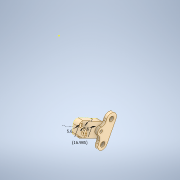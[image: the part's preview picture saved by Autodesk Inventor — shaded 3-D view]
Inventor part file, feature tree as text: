
AUTODESK INVENTOR PART (.ipt)
format: ipt  version: 2020 (Build 240168000, 168)  size: 313,344 bytes
history: native  units: in
note: dims shown in document units (in); Inventor stores cm internally (conversion verified against a paired STEP export)
features: sketch x11, extrude x7, fillet x4, projected_geometry x2
ambient origin geometry x8: Origin, YZ Plane, XZ Plane, XY Plane, X Axis, Y Axis, Z Axis, Center Point
bodies: Body1 (feature_tree)
feature tree (24):
  sketch  "Sketch3"  dims[d0=0.0039in d1=0.2362in d2=0.0in]
  sketch  "Sketch4"  dims[d3=0.315in d4=0.1575in d5=0.315in d6=0.0787in d7=0.0in d8=0.1181in]
  extrude  "Extrusion1"  Depth=0.2362in TaperAngle=0.0deg
  extrude  "Extrusion2"  Depth=0.1575in
  fillet  "Fillet1"  Radius=0.315in
  sketch  "Sketch7"  dims[d13=0.0787in d14=0.0787in d15=0.0in d16=0.2008in]
  fillet  "Fillet2"  Radius=0.0787in
  fillet  "Fillet3"  Radius=0.1181in
  extrude  "Extrusion3"  Depth=0.1181in
  extrude  "Extrusion4"  Depth=0.0787in
  sketch  "Sketch9"  dims[d22=0.3717in d23=0.0787in]
  sketch  "Sketch10"  dims[d27=0.1181in]
  sketch  "Sketch11"  dims[d29=0.1181in]
  extrude  "Extrusion6"  Depth=0.0787in TaperAngle=0.0deg
  fillet  "Fillet6"  Radius=0.2008in
  extrude  "Extrusion7"  Depth=0.1181in TaperAngle=0.0deg
  extrude  "Extrusion8"  Depth=0.0787in
  sketch  "Sketch5"  dims[d9=0.1102in d10=0.1181in]
  sketch  "Sketch6"  dims[d11=0.2047in d12=0.0787in]
  sketch  "Sketch8"  dims[d17=0.2008in d18=0.1181in d19=0.0in]
  projected_geometry  "Projected Loop2"
  projected_geometry  "Projected Loop3"
  sketch  "Sketch12"  dims[d30=0.315in]
  sketch  "Sketch13"  dims[d31=0.3937in d32=0.0in d33=0.1969in d34=0.1181in d35=0.0in d36=0.2205in d37=0.1378in d38=0.0in d39=0.2205in d40=0.6687in]
